# Revit family: Domotics-DomesticRanges-GEWISS-CHORUS_COMMAND-PUSH-BUTTON_NAME_PLATE
name_source: partatom
category: Apparecchi elettrici
revit_build: Autodesk Revit 2016 (Build: 20161004_0715(x64)
units: mm (PartAtom-declared; Revit-internal decimal feet)

## family parameters
Condiviso = Sì
Host = Superficie
Mantenere orientamento annotazione = Sì
Numero OmniClass = 23.80.50.11.14
Punto di calcolo locali = Sì
Quota connettore circolare = Usa diametro
Taglio con vuoti quando caricato = Sì
Tipo di parte = Normale
Titolo OmniClass = Switches

## types (6) — shared parameters
Bidimensionale = bidimensionale pulsanti TARGA : TRIPLO
Breaking capacity: = 1.25 In (200 position changes)
Catalogue = DOMOTICS
Catalogue Range = CHORUS - DOMESTIC RANGE
Category = Push-button with name plate
Description: = 1P NO - 10A
Electrocod = 0130
Glow Wire Test = 850°C
IDF = 576d2641-8241-4a29-981e-e24c3ef499ec
IDT = 4d45e74e-bdba-4c35-a76a-27be025ff1c1
Immagine tipo = GW14192.jpg
Insulation resistance = > 5 MOhm
Lamp = Cartridge lamp S6x36 mm
Lamp power = 2W
Lamp voltage = 12-24V ac/dc
Larghezza pulsante = 69 mm  [stored 0.226378 ft]
Number of poles = 1P
Produttore = GEWISS S.p.A.
Prolonged operation (no.of position changes) = 40.000 at In 250 V ac cosÃ˜=0,6
Prospetto di default = 1219 mm
Resistance at test voltage = 2000 V at 50 Hz for 1 minute
SEO = Push button
Simbolo_ = SIMBOLO PULSANTI : TARGA
Standard; = EN 60669-1
Technical sheet = https://www.gewiss.com
Terminal grip on cable traction = > 50 N
Terminal tightening capacity flexible cables (mm2) = min. 0,75 - max. 2x4
Terminal tightening capacity rigid cables (mm2) = min. 0,5 - max. 2x2,5
Thermo-pressure with ball = 125
Tipo_ = CHORUS PULSANTI TARGA_BASE : GW14192 - Titanio
Type = Name plate
Type of lamp = Cartridge lamp S6x36 mm
URL = https://www.gewiss.com
Version file RFA = 19.0
Voltage = 250 V ac
Voltage: = 250 V ac
Wiring terminals = With screw

## per-type parameters (varying)
| type | Colour | Descrizione | EAN code | Modello | No. Chorus modules |
| GW10191 - White | White | P-BUTTON 2M 1P NO 10A ILL NAME PL. WHITE | 8011564261884 | GW10191 | 2 |
| GW14192 - Titanium | Titanium | P-BUTTON 3M 1P NO 10A ILL NAME PLATE T | 8011564266230 | GW14192 | 3 |
| GW12192 - Black | Black | P-BUTTON 3M 1P NO 10A ILL NAME PL. BLACK | 8011564268890 | GW12192 | 3 |
| GW10192 - White | White | P-BUTTON 3M 1P NO 10A ILL NAME PL. WHITE | 8011564261907 | GW10192 | 3 |
| GW12191 - Black | Black | P-BUTTON 2M 1P NO 10A ILL NAME PL. BLACK | 8011564269491 | GW12191 | 2 |
| GW14191 - Titanium | Titanium | P-BUTTON 2M 1P NO 10A ILL NAME PLATE T | 8011564266223 | GW14191 | 2 |

note: source unit labels omitted for Thermo-pressure with ball — the stored unit's dimension contradicts the parameter name (converter mislabeling)

note: [stored X ft] marks values corroborated as IEEE doubles in the binary element streams (Revit-internal decimal feet)

## geometry (parser evidence)
native form markers: Sweep x2
no freeform markers — native parametric forms only
